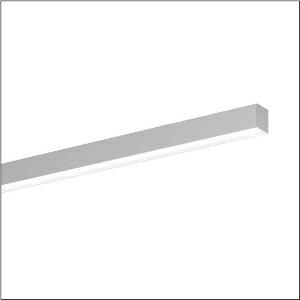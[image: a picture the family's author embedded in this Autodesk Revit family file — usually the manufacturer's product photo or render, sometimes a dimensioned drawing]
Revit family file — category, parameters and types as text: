
# Revit family: silica_r__21_51mx20da32sb_8410
name_source: partatom
category: Lighting Fixtures
units: mm (PartAtom-declared; Revit-internal decimal feet)

## family parameters
Cut with Voids When Loaded = No
Host = Face
Light Source = No
Part Type = Normal
Room Calculation Point = No
Round Connector Dimension = Use Diameter
Shared = No

## types (1)
- --- (1 x LED, 2400 lm, 16.1 W, 3000K)
    Apparent Load = 16 VA
    CIE Flux Codes = 48 79 96 100 100
    Color Rendering = 80
    Color Temperature = 3000K
    Default Elevation = 1800 mm
    Description = Silica® 21, office luminaire, primary optical cover: cover, of PMMA, opal, light emission: direct distribution, primary light characteristic: symmetric, installation type: surface-mounted, LED, rated luminous flux: 2.400lm, luminous efficacy: 149lm/W, light colour: 830, colour temperature: 3000K, with terminal, 3+2-pole, max. 2.5mm², mains connection: 220..240V, AC, 50/60Hz, rated input power: 16.1W, luminaire housing, of aluminium, metallic grey (RAL 9006), length: 1.204mm, width: 53mm, height: 53mm, protection rating (complete): IP20, insulation class (complete): insulation class I (protective earthing), certification: CE, permissible operating ambient temperature: 0..+35°C, standard: EN 50419, packaging unit: 1 piece
    Height = 0 mm  [stored 0 ft]
    Lamp = 1 x LED
    Lamp Light Flux = 2400 lm
    Lamp Power = 16.1 W
    Lamp count = 1
    Length = 1204 mm
    Luminous efficacy = 149 lm/W
    Manufacturer = Siteco
    ModVariant = No
    Model = 51MX20DA32SB
    Mounting Place = Ceiling
    Mounting Type = Recessed
    Number of Poles = 1
    OnlyDefault = Yes
    Power Factor = 1
    Product Name = Silica® 21
    Product group = office luminaire | ceiling recessed
    ProductGroupID = 401
    Protection Class = Protection class I
    Protection Degree = IP 20
    RLX_Detail_Level = 1
    RLX_Emergency_Light_Flux = 0 lm
    RLX_Emergency_Type = 0
    RLX_Emergency_Type_DB = No
    RlxData = <blob elided: 26217 chars, md5=6bdcb81d>
    Socket = socket
    Standby Power = 0 W
    System Light Flux = 2400 lm
    System Power = 16 W
    Type Comments = factory setting: luminous flux: 100 % | dim-lin: 254 | 233 mA
    Type Image = l_1313588.jpg
    URL = http://relux.com
    VarID = @adj_066327
    Voltage = 0 V
    Weight = 0.00 kg
    Width = 53 mm

note: [stored X ft] marks values corroborated as IEEE doubles in the binary element streams (Revit-internal decimal feet)

## geometry (parser evidence)
native form markers: Blend x4, Sweep x10
no freeform markers — native parametric forms only
